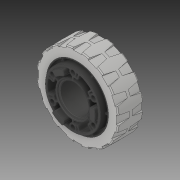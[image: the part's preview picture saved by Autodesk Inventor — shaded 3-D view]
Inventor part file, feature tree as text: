
AUTODESK INVENTOR PART (.ipt)
format: ipt  version: 2019 (Build 230136000, 136)  size: 3,040,768 bytes
history: native  units: in
note: dims shown in document units (in); Inventor stores cm internally (conversion verified against a paired STEP export)
features: fillet x1, pattern_circular x1
ambient origin geometry x8: Origin, YZ Plane, XZ Plane, XY Plane, X Axis, Y Axis, Z Axis, Center Point
bodies: Solid1 (feature_tree), Solid2 (feature_tree)
feature tree (2):
  fillet  "Fillet6"  [1 undecoded]
  pattern_circular  "CirPattern6"
note: 1 required parameter value undecoded (feature->parameter linkage not recoverable at this tier; creation-order binding heuristic only, values carry confidence <= 0.55)
